# Revit family: 201_EKE-RAS-2-_X_-_
name_source: partatom
category: Air Terminals
units: mm (PartAtom-declared; Revit-internal decimal feet)

## family parameters
Always vertical = Yes
Cut with Voids When Loaded = No
Part Type = Normal
Room Calculation Point = Yes
Round Connector Dimension = Use Diameter
Shared = No
Work Plane-Based = No

## types (12) — shared parameters
CAT0 = Yes
CL_Location_5000 = 5000 mm  [stored 16.4042 ft]
CON1 = No
CON2 = Yes
Description = Supply grille with plenum box, rear connection
L_ARR = 400 mm  [stored 1.31234 ft]
Manufacturer = Climecon
QmdConnectorList = 201;D
URL = www.climecon.fi
W1 = 5 mm  [stored 0.0164042 ft]
W_ARR = 400 mm  [stored 1.31234 ft]
XRefLineVPlnId = 7453
YRefLineVPlnId = 7456
magiPartTypeId = 201
magiProductFamilyId = EKE-RAS-2-*X*-*
zero-valued in all types: CLBTZ, H_ARR, MC_Default_elevation

## per-type parameters (varying)
| type | BB1 | BB2 | BB3 | BH3 | D | E | EF1 | E__ve | HH1 | HH2 |
| EKE-RAS-2-200x100-125 | 113 mm  [stored 0.370735 ft] | 100 mm  [stored 0.328084 ft] | 150 mm  [stored 0.492126 ft] | 95 mm  [stored 0.31168 ft] | 125 mm | 270 mm  [stored 0.885827 ft] | 167 mm  [stored 0.5479 ft] | -270 mm  [stored -0.885827 ft] | 63 mm  [stored 0.206693 ft] | 50 mm  [stored 0.164042 ft] |
| EKE-RAS-2-800x200-315 | 413 mm  [stored 1.35499 ft] | 400 mm  [stored 1.31234 ft] | 450 mm  [stored 1.47638 ft] | 178 mm | 315 mm | 470 mm  [stored 1.54199 ft] | 273 mm  [stored 0.895669 ft] | -470 mm  [stored -1.54199 ft] | 113 mm  [stored 0.370735 ft] | 100 mm  [stored 0.328084 ft] |
| EKE-RAS-2-600x200-315 | 313 mm  [stored 1.0269 ft] | 300 mm  [stored 0.984252 ft] | 350 mm  [stored 1.14829 ft] | 178 mm | 315 mm | 470 mm  [stored 1.54199 ft] | 273 mm  [stored 0.895669 ft] | -470 mm  [stored -1.54199 ft] | 113 mm  [stored 0.370735 ft] | 100 mm  [stored 0.328084 ft] |
| EKE-RAS-2-500x200-315 | 263 mm  [stored 0.862861 ft] | 250 mm  [stored 0.82021 ft] | 300 mm  [stored 0.984252 ft] | 178 mm | 315 mm | 470 mm  [stored 1.54199 ft] | 273 mm  [stored 0.895669 ft] | -470 mm  [stored -1.54199 ft] | 113 mm  [stored 0.370735 ft] | 100 mm  [stored 0.328084 ft] |
| EKE-RAS-2-600x150-250 | 313 mm  [stored 1.0269 ft] | 300 mm  [stored 0.984252 ft] | 350 mm  [stored 1.14829 ft] | 145 mm  [stored 0.475722 ft] | 250 mm | 400 mm  [stored 1.31234 ft] | 235 mm  [stored 0.770997 ft] | -400 mm  [stored -1.31234 ft] | 88 mm  [stored 0.288714 ft] | 75 mm  [stored 0.246063 ft] |
| EKE-RAS-2-500x150-250 | 263 mm  [stored 0.862861 ft] | 250 mm  [stored 0.82021 ft] | 300 mm  [stored 0.984252 ft] | 145 mm  [stored 0.475722 ft] | 250 mm | 400 mm  [stored 1.31234 ft] | 235 mm  [stored 0.770997 ft] | -400 mm  [stored -1.31234 ft] | 88 mm  [stored 0.288714 ft] | 75 mm  [stored 0.246063 ft] |
| EKE-RAS-2-400x200-250 | 213 mm  [stored 0.698819 ft] | 200 mm  [stored 0.656168 ft] | 250 mm  [stored 0.82021 ft] | 145 mm  [stored 0.475722 ft] | 250 mm | 400 mm  [stored 1.31234 ft] | 235 mm  [stored 0.770997 ft] | -400 mm  [stored -1.31234 ft] | 113 mm  [stored 0.370735 ft] | 100 mm  [stored 0.328084 ft] |
| EKE-RAS-2-400x150-250 | 213 mm  [stored 0.698819 ft] | 200 mm  [stored 0.656168 ft] | 250 mm  [stored 0.82021 ft] | 145 mm  [stored 0.475722 ft] | 250 mm | 400 mm  [stored 1.31234 ft] | 235 mm  [stored 0.770997 ft] | -400 mm  [stored -1.31234 ft] | 88 mm  [stored 0.288714 ft] | 75 mm  [stored 0.246063 ft] |
| EKE-RAS-2-300x200-250 | 163 mm  [stored 0.534777 ft] | 150 mm  [stored 0.492126 ft] | 200 mm  [stored 0.656168 ft] | 145 mm  [stored 0.475722 ft] | 250 mm | 400 mm  [stored 1.31234 ft] | 235 mm  [stored 0.770997 ft] | -400 mm  [stored -1.31234 ft] | 113 mm  [stored 0.370735 ft] | 100 mm  [stored 0.328084 ft] |
| EKE-RAS-2-300x150-200 | 163 mm  [stored 0.534777 ft] | 150 mm  [stored 0.492126 ft] | 200 mm  [stored 0.656168 ft] | 125 mm  [stored 0.410105 ft] | 200 mm | 350 mm  [stored 1.14829 ft] | 210 mm  [stored 0.688976 ft] | -350 mm  [stored -1.14829 ft] | 88 mm  [stored 0.288714 ft] | 75 mm  [stored 0.246063 ft] |
| EKE-RAS-2-400x100-160 | 213 mm  [stored 0.698819 ft] | 200 mm  [stored 0.656168 ft] | 250 mm  [stored 0.82021 ft] | 110 mm  [stored 0.360892 ft] | 160 mm | 310 mm  [stored 1.01706 ft] | 190 mm  [stored 0.62336 ft] | -310 mm  [stored -1.01706 ft] | 63 mm  [stored 0.206693 ft] | 50 mm  [stored 0.164042 ft] |
| EKE-RAS-2-300x100-160 | 163 mm  [stored 0.534777 ft] | 150 mm  [stored 0.492126 ft] | 200 mm  [stored 0.656168 ft] | 110 mm  [stored 0.360892 ft] | 160 mm | 310 mm  [stored 1.01706 ft] | 190 mm  [stored 0.62336 ft] | -310 mm  [stored -1.01706 ft] | 63 mm  [stored 0.206693 ft] | 50 mm  [stored 0.164042 ft] |

note: column(s) folded — value = type name in every type: magiProductCode, magiProductId

note: [stored X ft] marks values corroborated as IEEE doubles in the binary element streams (Revit-internal decimal feet)

## geometry (parser evidence)
native form markers: Sweep x1
no freeform markers — native parametric forms only
